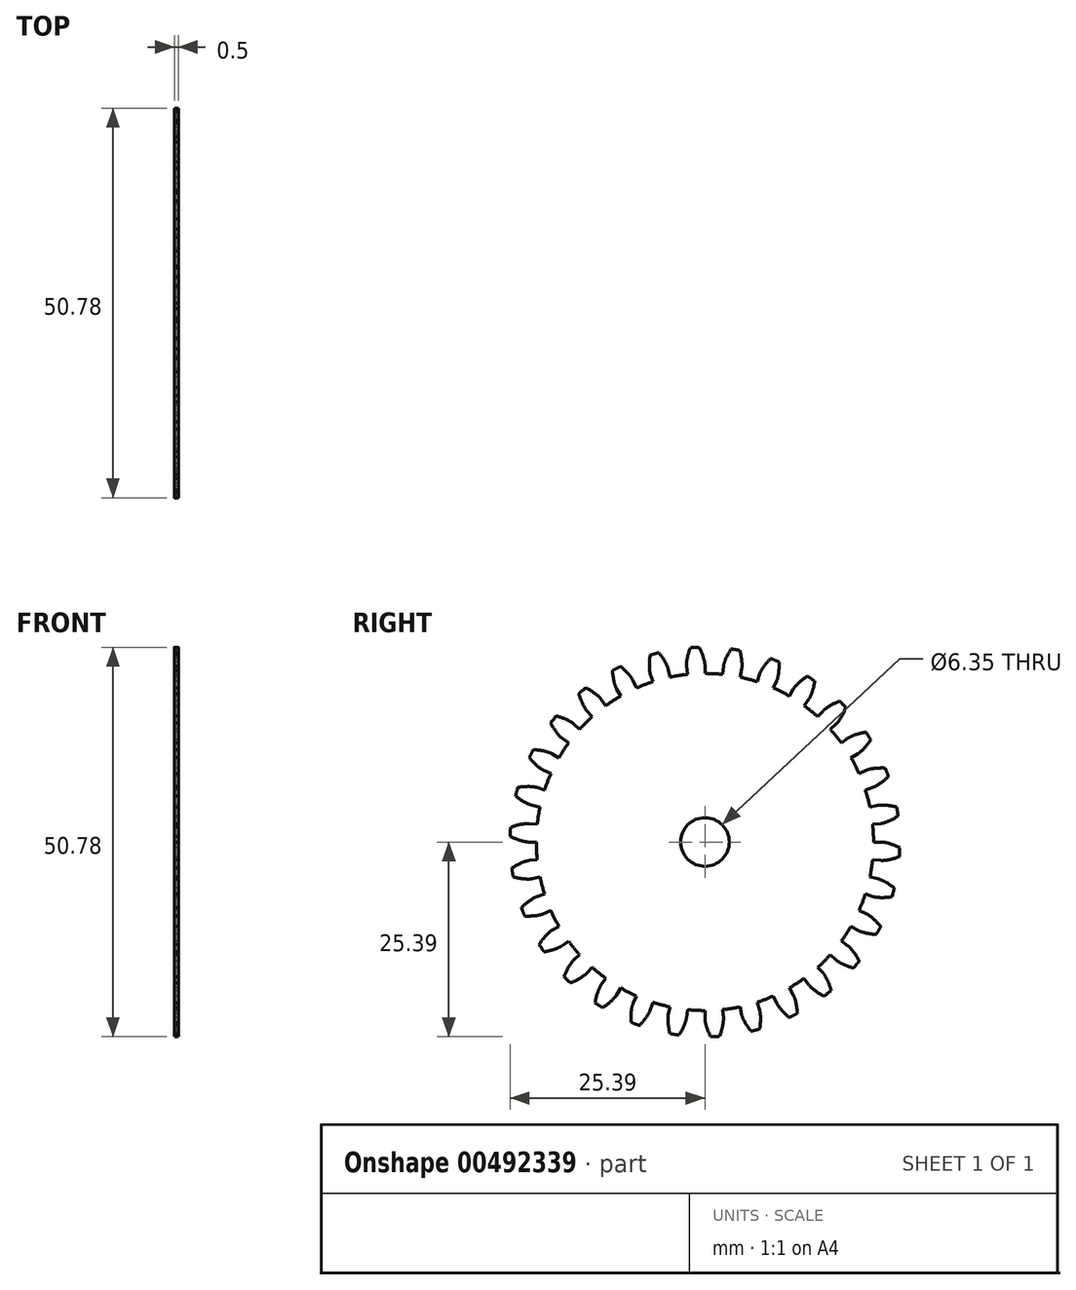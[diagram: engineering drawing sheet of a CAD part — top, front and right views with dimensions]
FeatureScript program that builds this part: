
annotation { "Feature Type Name" : "Feature", "Feature Type Description" : "" }
export const myFeature = defineFeature(function(context is Context, id is Id, definition is map)
    precondition{}
    {
        {
            assignVariable(context, id + "F0", {"name" : "NumberTeeth", "anyValue" : 30});
        }
        {
            assignVariable(context, id + "F1", {"name" : "GearThickness", "anyValue" : .5});
        }
        {
            var Q0;
            Q0=qCreatedBy(makeId("Right.planeOp"),FACE);
            var sketch = newSketch(context, id + "F2", { "sketchPlane" : qUnion([Q0])});
            skCircle(sketch, "E0", {"center": v(0, 0) * mm, "radius": 21.98 * mm});
            skCircle(sketch, "E1", {"center": v(0, 0) * mm, "radius": 23.05 * mm, "construction": true});
            skCircle(sketch, "E2", {"center": v(0, 0) * mm, "radius": 23.81 * mm, "construction": true});
            skCircle(sketch, "E3", {"center": v(0, 0) * mm, "radius": 25.4 * mm});
            skLineSegment(sketch, "E4", {"start": v(0, 0) * mm, "end": v(-23.05, 0) * mm, "construction": true});
            skLineSegment(sketch, "E5.1.0", {"start": v(0, 0) * mm, "end": v(-23.03, 1.15) * mm, "construction": true});
            skLineSegment(sketch, "E5.2.0", {"start": v(0, 0) * mm, "end": v(-22.94, 2.3) * mm, "construction": true});
            skLineSegment(sketch, "E5.3.0", {"start": v(0, 0) * mm, "end": v(-22.8, 3.45) * mm, "construction": true});
            skLineSegment(sketch, "E5.4.0", {"start": v(0, 0) * mm, "end": v(-22.6, 4.58) * mm, "construction": true});
            skLineSegment(sketch, "E5.5.0", {"start": v(0, 0) * mm, "end": v(-22.34, 5.7) * mm, "construction": true});
            skLineSegment(sketch, "E5.6.0", {"start": v(0, 0) * mm, "end": v(-22.02, 6.81) * mm, "construction": true});
            skLineSegment(sketch, "E5.7.0", {"start": v(0, 0) * mm, "end": v(-21.66, 7.9) * mm, "construction": true});
            skLineSegment(sketch, "E5.8.0", {"start": v(0, 0) * mm, "end": v(-21.23, 8.98) * mm, "construction": true});
            skLineSegment(sketch, "E5.9.0", {"start": v(0, 0) * mm, "end": v(-20.76, 10.03) * mm, "construction": true});
            skLineSegment(sketch, "E5.10.0", {"start": v(0, 0) * mm, "end": v(-20.23, 11.05) * mm, "construction": true});
            skLineSegment(sketch, "E5.11.0", {"start": v(0, 0) * mm, "end": v(-19.65, 12.05) * mm, "construction": true});
            skLineSegment(sketch, "E5.12.0", {"start": v(0, 0) * mm, "end": v(-19.03, 13.02) * mm, "construction": true});
            skLineSegment(sketch, "E5.13.0", {"start": v(0, 0) * mm, "end": v(-18.35, 13.95) * mm, "construction": true});
            skLineSegment(sketch, "E5.14.0", {"start": v(0, 0) * mm, "end": v(-17.63, 14.85) * mm});
            skLineSegment(sketch, "E5.anchor2", {"start": v(0, 0) * mm, "end": v(-17.63, 14.85) * mm, "construction": true});
            skLineSegment(sketch, "E6", {"start": v(-23.03, 1.15) * mm, "end": v(-23.08, 0) * mm, "construction": true});
            skLineSegment(sketch, "E7", {"start": v(-22.94, 2.3) * mm, "end": v(-23.17, 0) * mm, "construction": true});
            skLineSegment(sketch, "E8", {"start": v(-22.8, 3.45) * mm, "end": v(-23.31, 0.03) * mm, "construction": true});
            skLineSegment(sketch, "E9", {"start": v(-22.34, 5.7) * mm, "end": v(-23.76, 0.12) * mm, "construction": true});
            skLineSegment(sketch, "E10", {"start": v(-22.02, 6.81) * mm, "end": v(-24.07, 0.2) * mm, "construction": true});
            skLineSegment(sketch, "E11", {"start": v(-21.66, 7.9) * mm, "end": v(-24.42, 0.33) * mm, "construction": true});
            skLineSegment(sketch, "E12", {"start": v(-21.23, 8.98) * mm, "end": v(-24.83, 0.48) * mm, "construction": true});
            skLineSegment(sketch, "E13", {"start": v(-20.76, 10.03) * mm, "end": v(-25.27, 0.69) * mm, "construction": true});
            skLineSegment(sketch, "E14", {"start": v(-20.23, 11.05) * mm, "end": v(-25.76, 0.94) * mm, "construction": true});
            skLineSegment(sketch, "E15", {"start": v(-19.65, 12.05) * mm, "end": v(-26.28, 1.24) * mm, "construction": true});
            skLineSegment(sketch, "E16", {"start": v(-22.6, 4.58) * mm, "end": v(-23.51, 0.06) * mm, "construction": true});
            skLineSegment(sketch, "E17", {"start": v(-19.03, 13.02) * mm, "end": v(-26.84, 1.6) * mm, "construction": true});
            skLineSegment(sketch, "E18", {"start": v(-18.35, 13.95) * mm, "end": v(-27.42, 2.02) * mm, "construction": true});
            skLineSegment(sketch, "E19", {"start": v(-17.63, 14.85) * mm, "end": v(-28.03, 2.5) * mm, "construction": true});
            skLineSegment(sketch, "E20", {"start": v(0, 0) * mm, "end": v(-23.02, 1.2) * mm, "construction": true});
            skLineSegment(sketch, "E21", {"start": v(-21.98, 0) * mm, "end": v(-23.05, 0) * mm});
            skLineSegment(sketch, "E22.MirrorCS", {"start": v(-21.86, 2.3) * mm, "end": v(-22.93, 2.4) * mm});
            skFitSpline(sketch, "E23", {"points": [v(-23.05, 0) * mm, v(-23.08, 0) * mm, v(-23.17, 0) * mm, v(-23.31, 0.03) * mm, v(-23.51, 0.06) * mm, v(-23.76, 0.12) * mm, v(-24.07, 0.2) * mm, v(-24.42, 0.33) * mm, v(-24.83, 0.48) * mm, v(-25.27, 0.69) * mm, v(-25.76, 0.94) * mm, v(-26.28, 1.24) * mm, v(-26.84, 1.6) * mm, v(-27.42, 2.02) * mm, v(-28.03, 2.5) * mm], "startDerivative": vector(-0.76, 0) * mm, "endDerivative": vector(-1.4, 1.18) * mm});
            skLineSegment(sketch, "E24", {"start": v(-22.5, -2.14) * mm, "end": v(-28.03, 2.5) * mm, "construction": true});
            skFitSpline(sketch, "E25.MirrorCS", {"points": [v(-22.93, 2.4) * mm, v(-22.96, 2.41) * mm, v(-23.04, 2.41) * mm, v(-23.19, 2.41) * mm, v(-23.39, 2.4) * mm, v(-23.65, 2.37) * mm, v(-23.96, 2.31) * mm, v(-24.32, 2.23) * mm, v(-24.74, 2.11) * mm, v(-25.2, 1.96) * mm, v(-25.71, 1.76) * mm, v(-26.27, 1.51) * mm, v(-26.86, 1.21) * mm, v(-27.48, 0.85) * mm, v(-28.14, 0.43) * mm], "startDerivative": vector(-0.76, 0.08) * mm, "endDerivative": vector(-1.52, -1.03) * mm});
            skSolve(sketch);
        }
        {
            var Q0;
            {var subQ0=sQuery(id+"F2.wireOp",EDGE,"E0");var subQ27=makeQuery(id+"F2.imprint","INTERSECT",VERTEX,{"derivedFrom":[subQ0,sQuery(id+"F2.wireOp",EDGE,"10ea1024-8cf5-41f5-a75f-a634b86921f3.10.0")]});Q0=makeQuery(id+"F2.imprint","IMPRINT",FACE,{"disambiguationData":[TD([[makeQuery(id+"F2.imprint","IMPRINT",EDGE,{"disambiguationData":[TD([[subQ27,-1.0]])],"derivedFrom":subQ0}),1.0]])]});}
            var Q1;
            {var subQ0=sQuery(id+"F2.wireOp",EDGE,"10ea1024-8cf5-41f5-a75f-a634b86921f3.1.0");Q1=makeQuery(id+"F2.imprint","IMPRINT",FACE,{"disambiguationData":[TD([[makeQuery(id+"F2.imprint","IMPRINT",EDGE,{"derivedFrom":subQ0}),-1.0]])]});}
            var Q2;
            {var subQ7=sQuery(id+"F2.wireOp",EDGE,"10ea1024-8cf5-41f5-a75f-a634b86921f3.2.0");Q2=makeQuery(id+"F2.imprint","IMPRINT",FACE,{"disambiguationData":[TD([[makeQuery(id+"F2.imprint","IMPRINT",EDGE,{"derivedFrom":subQ7}),-1.0]])]});}
            var Q3;
            {var subQ8=sQuery(id+"F2.wireOp",EDGE,"10ea1024-8cf5-41f5-a75f-a634b86921f3.3.0");Q3=makeQuery(id+"F2.imprint","IMPRINT",FACE,{"disambiguationData":[TD([[makeQuery(id+"F2.imprint","IMPRINT",EDGE,{"derivedFrom":subQ8}),-1.0]])]});}
            var Q4;
            {var subQ2=sQuery(id+"F2.wireOp",EDGE,"10ea1024-8cf5-41f5-a75f-a634b86921f3.4.0");Q4=makeQuery(id+"F2.imprint","IMPRINT",FACE,{"disambiguationData":[TD([[makeQuery(id+"F2.imprint","IMPRINT",EDGE,{"derivedFrom":subQ2}),-1.0]])]});}
            var Q5;
            {var subQ8=sQuery(id+"F2.wireOp",EDGE,"10ea1024-8cf5-41f5-a75f-a634b86921f3.5.0");Q5=makeQuery(id+"F2.imprint","IMPRINT",FACE,{"disambiguationData":[TD([[makeQuery(id+"F2.imprint","IMPRINT",EDGE,{"derivedFrom":subQ8}),-1.0]])]});}
            var Q6;
            {var subQ3=sQuery(id+"F2.wireOp",EDGE,"10ea1024-8cf5-41f5-a75f-a634b86921f3.6.0");Q6=makeQuery(id+"F2.imprint","IMPRINT",FACE,{"disambiguationData":[TD([[makeQuery(id+"F2.imprint","IMPRINT",EDGE,{"derivedFrom":subQ3}),-1.0]])]});}
            var Q7;
            {var subQ0=sQuery(id+"F2.wireOp",EDGE,"10ea1024-8cf5-41f5-a75f-a634b86921f3.7.0");Q7=makeQuery(id+"F2.imprint","IMPRINT",FACE,{"disambiguationData":[TD([[makeQuery(id+"F2.imprint","IMPRINT",EDGE,{"derivedFrom":subQ0}),-1.0]])]});}
            var Q8;
            {var subQ5=sQuery(id+"F2.wireOp",EDGE,"10ea1024-8cf5-41f5-a75f-a634b86921f3.8.0");Q8=makeQuery(id+"F2.imprint","IMPRINT",FACE,{"disambiguationData":[TD([[makeQuery(id+"F2.imprint","IMPRINT",EDGE,{"derivedFrom":subQ5}),-1.0]])]});}
            var Q9;
            {var subQ1=sQuery(id+"F2.wireOp",EDGE,"10ea1024-8cf5-41f5-a75f-a634b86921f3.9.0");Q9=makeQuery(id+"F2.imprint","IMPRINT",FACE,{"disambiguationData":[TD([[makeQuery(id+"F2.imprint","IMPRINT",EDGE,{"derivedFrom":subQ1}),-1.0]])]});}
            var Q10;
            {var subQ5=sQuery(id+"F2.wireOp",EDGE,"10ea1024-8cf5-41f5-a75f-a634b86921f3.10.0");Q10=makeQuery(id+"F2.imprint","IMPRINT",FACE,{"disambiguationData":[TD([[makeQuery(id+"F2.imprint","IMPRINT",EDGE,{"derivedFrom":subQ5}),-1.0]])]});}
            var Q11;
            {var subQ8=sQuery(id+"F2.wireOp",EDGE,"10ea1024-8cf5-41f5-a75f-a634b86921f3.11.0");Q11=makeQuery(id+"F2.imprint","IMPRINT",FACE,{"disambiguationData":[TD([[makeQuery(id+"F2.imprint","IMPRINT",EDGE,{"derivedFrom":subQ8}),-1.0]])]});}
            var Q12;
            {var subQ2=sQuery(id+"F2.wireOp",EDGE,"10ea1024-8cf5-41f5-a75f-a634b86921f3.12.0");Q12=makeQuery(id+"F2.imprint","IMPRINT",FACE,{"disambiguationData":[TD([[makeQuery(id+"F2.imprint","IMPRINT",EDGE,{"derivedFrom":subQ2}),-1.0]])]});}
            var Q13;
            {var subQ3=sQuery(id+"F2.wireOp",EDGE,"10ea1024-8cf5-41f5-a75f-a634b86921f3.13.0");Q13=makeQuery(id+"F2.imprint","IMPRINT",FACE,{"disambiguationData":[TD([[makeQuery(id+"F2.imprint","IMPRINT",EDGE,{"derivedFrom":subQ3}),-1.0]])]});}
            var Q14;
            {var subQ0=sQuery(id+"F2.wireOp",EDGE,"10ea1024-8cf5-41f5-a75f-a634b86921f3.14.0");Q14=makeQuery(id+"F2.imprint","IMPRINT",FACE,{"disambiguationData":[TD([[makeQuery(id+"F2.imprint","IMPRINT",EDGE,{"derivedFrom":subQ0}),-1.0]])]});}
            var Q15;
            {var subQ6=sQuery(id+"F2.wireOp",EDGE,"10ea1024-8cf5-41f5-a75f-a634b86921f3.15.0");Q15=makeQuery(id+"F2.imprint","IMPRINT",FACE,{"disambiguationData":[TD([[makeQuery(id+"F2.imprint","IMPRINT",EDGE,{"derivedFrom":subQ6}),-1.0]])]});}
            var Q16;
            {var subQ5=sQuery(id+"F2.wireOp",EDGE,"10ea1024-8cf5-41f5-a75f-a634b86921f3.16.0");Q16=makeQuery(id+"F2.imprint","IMPRINT",FACE,{"disambiguationData":[TD([[makeQuery(id+"F2.imprint","IMPRINT",EDGE,{"derivedFrom":subQ5}),-1.0]])]});}
            var Q17;
            {var subQ7=sQuery(id+"F2.wireOp",EDGE,"10ea1024-8cf5-41f5-a75f-a634b86921f3.17.0");Q17=makeQuery(id+"F2.imprint","IMPRINT",FACE,{"disambiguationData":[TD([[makeQuery(id+"F2.imprint","IMPRINT",EDGE,{"derivedFrom":subQ7}),-1.0]])]});}
            var Q18;
            {var subQ5=sQuery(id+"F2.wireOp",EDGE,"10ea1024-8cf5-41f5-a75f-a634b86921f3.18.0");Q18=makeQuery(id+"F2.imprint","IMPRINT",FACE,{"disambiguationData":[TD([[makeQuery(id+"F2.imprint","IMPRINT",EDGE,{"derivedFrom":subQ5}),-1.0]])]});}
            var Q19;
            {var subQ8=sQuery(id+"F2.wireOp",EDGE,"10ea1024-8cf5-41f5-a75f-a634b86921f3.19.0");Q19=makeQuery(id+"F2.imprint","IMPRINT",FACE,{"disambiguationData":[TD([[makeQuery(id+"F2.imprint","IMPRINT",EDGE,{"derivedFrom":subQ8}),-1.0]])]});}
            var Q20;
            {var subQ8=sQuery(id+"F2.wireOp",EDGE,"E21");Q20=makeQuery(id+"F2.imprint","IMPRINT",FACE,{"disambiguationData":[TD([[makeQuery(id+"F2.imprint","IMPRINT",EDGE,{"derivedFrom":subQ8}),-1.0]])]});}
            extrude(context, id + "F3", {"entities" : qUnion([Q0, Q1, Q2, Q3, Q4, Q5, Q6, Q7, Q8, Q9, Q10, Q11, Q12, Q13, Q14, Q15, Q16, Q17, Q18, Q19, Q20]), "depth" : (getVariable(context, 'GearThickness')) * mm});
        }
        {
            var Q0;
            Q0=makeQuery(id+"F3.opExtrude","SWEPT_FACE",FACE,{"disambiguationData":[OSD([sQuery(id+"F2.wireOp",EDGE,"E25.MirrorCS")])]});
            var Q1;
            Q1=makeQuery(id+"F3.opExtrude","SWEPT_FACE",FACE,{"disambiguationData":[OSD([sQuery(id+"F2.wireOp",EDGE,"E23")])]});
            var Q2;
            Q2=makeQuery(id+"F3.opExtrude","SWEPT_FACE",FACE,{"disambiguationData":[OSD([sQuery(id+"F2.wireOp",EDGE,"E3")])]});
            var Q3;
            Q3=makeQuery(id+"F3.opExtrude","SWEPT_FACE",FACE,{"disambiguationData":[OSD([sQuery(id+"F2.wireOp",EDGE,"E22.MirrorCS")])]});
            var Q4;
            Q4=makeQuery(id+"F3.opExtrude","SWEPT_FACE",FACE,{"disambiguationData":[OSD([sQuery(id+"F2.wireOp",EDGE,"E21")])]});
            var Q5;
            Q5=makeQuery(id+"F3.opExtrude","SWEPT_FACE",FACE,{"disambiguationData":[OSD([sQuery(id+"F2.wireOp",EDGE,"E0")])]});
            circularPattern(context, id + "F4", {"faces" : qUnion([Q0, Q1, Q2, Q3, Q4]), "axis" : qUnion([Q5]), "angle" : 360 * degree, "instanceCount" : getVariable(context, 'NumberTeeth'), "equalSpace" : true, "patternType" : PatternType.FACE});
        }
        {
            var Q0;
            {var subQ0=sQuery(id+"F2.wireOp",EDGE,"E0");var subQ2=makeQuery(id+"F2.imprint","IMPRINT",VERTEX,{"derivedFrom":subQ0});Q0=makeQuery(id+"F2.imprint","IMPRINT",FACE,{"disambiguationData":[TD([[makeQuery(id+"F2.imprint","IMPRINT",EDGE,{"disambiguationData":[TD([[subQ2,-1.0]])],"derivedFrom":subQ0}),1.0]])]});}
            var sketch = newSketch(context, id + "F5", { "sketchPlane" : qUnion([Q0])});
            skPoint(sketch, "E26", {"position": v(0, 0) * mm});
            skSolve(sketch);
        }
        {
            var Q0;
            Q0=sQuery(id+"F5.wireOp",VERTEX,"E26");
            var Q1;
            Q1=makeQuery(id+"F3.opExtrude","SWEPT_BODY",BODY,{"disambiguationData":[OSD([sQuery(id+"F2.wireOp",EDGE,"E0"),sQuery(id+"F2.wireOp",EDGE,"E3"),sQuery(id+"F2.wireOp",EDGE,"E21"),sQuery(id+"F2.wireOp",EDGE,"E22.MirrorCS"),sQuery(id+"F2.wireOp",EDGE,"E23"),sQuery(id+"F2.wireOp",EDGE,"E25.MirrorCS")])]});
            hole(context, id + "F6", {"style" : HoleStyle.SIMPLE, "endStyle" : HoleEndStyle.THROUGH, "oppositeDirection" : true, "holeDiameter" : 6.35 * mm, "isTappedThrough" : true, "tappedDepth" : 12.7 * mm, "tapClearance" : 3, "locations" : qUnion([Q0]), "scope" : qUnion([Q1])});
        }
    });
